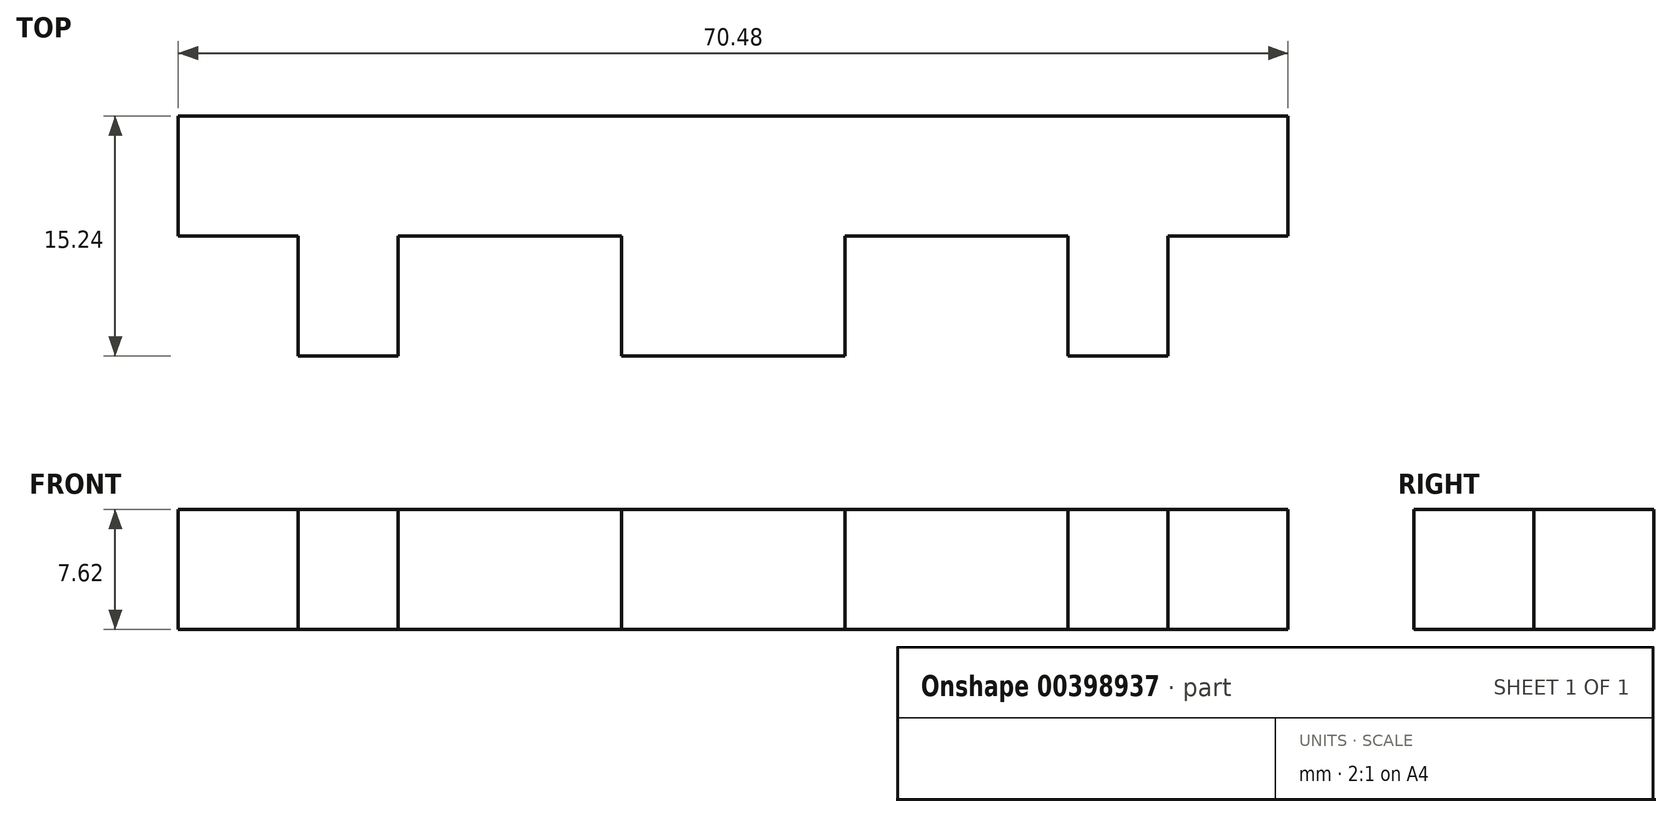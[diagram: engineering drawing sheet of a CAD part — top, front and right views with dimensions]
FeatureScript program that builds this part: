
annotation { "Feature Type Name" : "Feature", "Feature Type Description" : "" }
export const myFeature = defineFeature(function(context is Context, id is Id, definition is map)
    precondition{}
    {
        {
            var Q0;
            Q0=qCreatedBy(makeId("Top.planeOp"),FACE);
            var sketch = newSketch(context, id + "F0", { "sketchPlane" : qUnion([Q0])});
            skLineSegment(sketch, "E0.bottom", {"start": v(0, 0) * mm, "end": v(70.48, 0) * mm});
            skLineSegment(sketch, "E0.top", {"start": v(7.62, -15.24) * mm, "end": v(13.97, -15.24) * mm});
            skLineSegment(sketch, "E0.left", {"start": v(0, 0) * mm, "end": v(0, -7.62) * mm});
            skLineSegment(sketch, "E0.right", {"start": v(70.48, 0) * mm, "end": v(70.48, -7.62) * mm});
            skLineSegment(sketch, "E1", {"start": v(0, -7.62) * mm, "end": v(7.62, -7.62) * mm});
            skLineSegment(sketch, "E2", {"start": v(7.62, -7.62) * mm, "end": v(7.62, -15.24) * mm});
            skLineSegment(sketch, "E3", {"start": v(13.97, -15.24) * mm, "end": v(13.97, -7.62) * mm});
            skPoint(sketch, "E4.orphan", {"position": v(0, -15.24) * mm});
            skLineSegment(sketch, "E5", {"start": v(13.97, -7.62) * mm, "end": v(28.16, -7.62) * mm});
            skLineSegment(sketch, "E6", {"start": v(28.16, -7.62) * mm, "end": v(28.16, -15.24) * mm});
            skLineSegment(sketch, "E7", {"start": v(28.16, -15.24) * mm, "end": v(42.33, -15.24) * mm});
            skLineSegment(sketch, "E8", {"start": v(42.33, -15.24) * mm, "end": v(42.33, -7.62) * mm});
            skLineSegment(sketch, "E9", {"start": v(42.33, -7.62) * mm, "end": v(56.52, -7.62) * mm});
            skLineSegment(sketch, "E10", {"start": v(56.52, -7.62) * mm, "end": v(56.52, -15.24) * mm});
            skLineSegment(sketch, "E11", {"start": v(56.52, -15.24) * mm, "end": v(62.87, -15.24) * mm});
            skLineSegment(sketch, "E12", {"start": v(62.87, -15.24) * mm, "end": v(62.87, -7.62) * mm});
            skLineSegment(sketch, "E13", {"start": v(62.87, -7.62) * mm, "end": v(70.48, -7.62) * mm});
            skSolve(sketch);
        }
        {
            var Q0;
            Q0=makeQuery(id+"F0.imprint","IMPRINT",FACE,{"disambiguationData":[TD([[makeQuery(id+"F0.imprint","IMPRINT",EDGE,{"derivedFrom":sQuery(id+"F0.wireOp",EDGE,"E0.bottom")}),-1.0]])]});
            extrude(context, id + "F1", {"entities" : qUnion([Q0]), "depth" : 7.62 * mm, "offsetDistance" : 25.4 * mm});
        }
    });
